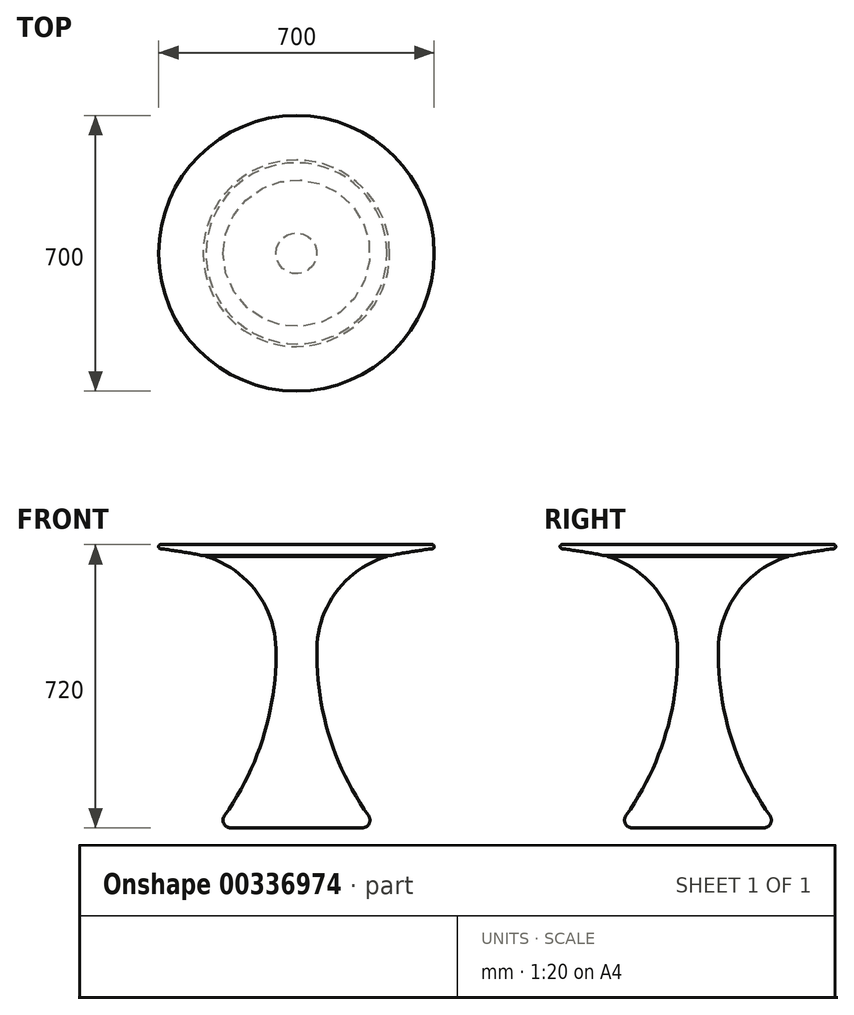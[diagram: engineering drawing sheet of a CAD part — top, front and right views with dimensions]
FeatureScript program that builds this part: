
annotation { "Feature Type Name" : "Feature", "Feature Type Description" : "" }
export const myFeature = defineFeature(function(context is Context, id is Id, definition is map)
    precondition{}
    {
        {
            var Q0;
            Q0=qCreatedBy(makeId("Front.planeOp"),FACE);
            var sketch = newSketch(context, id + "F0", { "sketchPlane" : qUnion([Q0])});
            skSolve(sketch);
        }
        {
            var Q0;
            Q0=qCreatedBy(makeId("Front.planeOp"),FACE);
            var sketch = newSketch(context, id + "F1", { "sketchPlane" : qUnion([Q0])});
            skLineSegment(sketch, "E0", {"start": v(350, 690) * mm, "end": v(120, 690) * mm});
            skLineSegment(sketch, "E1", {"start": v(350, 0) * mm, "end": v(350, 690) * mm});
            skLineSegment(sketch, "E2", {"start": v(350, 0) * mm, "end": v(183.46, 0) * mm});
            skArc(sketch, "E3", {"start": v(298, 455) * mm, "mid": v(247.32, 601.53) * mm, "end": v(120, 690) * mm});
            skArc(sketch, "E4", {"start": v(167.15, 31.57) * mm, "mid": v(266.46, 232.82) * mm, "end": v(298, 455) * mm});
            skPoint(sketch, "E5.visualSharp", {"position": v(143.4, 0) * mm});
            skArc(sketch, "E5.filletArc", {"start": v(167.15, 31.57) * mm, "mid": v(165.69, 10.82) * mm, "end": v(183.46, 0) * mm});
            skSolve(sketch);
        }
        {
            var Q0;
            Q0=qCreatedBy(makeId("Front.planeOp"),FACE);
            var sketch = newSketch(context, id + "F2", { "sketchPlane" : qUnion([Q0])});
            skLineSegment(sketch, "E6.0", {"start": v(350, 0) * mm, "end": v(350, 690) * mm});
            skSolve(sketch);
        }
        {
            var Q0;
            Q0 = qSketchRegion(id + "F1", true);
            var Q1;
            Q1=sQuery(id+"F2.wireOp",EDGE,"E6.0");
            revolve(context, id + "F3", {"entities" : qUnion([Q0]), "axis" : qUnion([Q1]), "revolveType" : RevolveType.FULL});
        }
        {
            var Q0;
            Q0=qCreatedBy(makeId("Front.planeOp"),FACE);
            var sketch = newSketch(context, id + "F4", { "sketchPlane" : qUnion([Q0])});
            skLineSegment(sketch, "E7", {"start": v(350, 720) * mm, "end": v(5, 720) * mm});
            skLineSegment(sketch, "E8", {"start": v(350, 720) * mm, "end": v(350, 692) * mm});
            skLineSegment(sketch, "E9", {"start": v(350, 692) * mm, "end": v(112.98, 692) * mm});
            skArc(sketch, "E10", {"start": v(112.98, 692) * mm, "mid": v(58.83, 701.66) * mm, "end": v(4.38, 709.46) * mm});
            skLineSegment(sketch, "E11", {"start": v(0, 715) * mm, "end": v(0, 714.42) * mm});
            skPoint(sketch, "E12.visualSharp", {"position": v(0, 710) * mm});
            skArc(sketch, "E12.filletArc", {"start": v(0, 714.42) * mm, "mid": v(1.25, 711.1) * mm, "end": v(4.38, 709.46) * mm});
            skPoint(sketch, "E13.visualSharp", {"position": v(0, 720) * mm});
            skArc(sketch, "E13.filletArc", {"start": v(5, 720) * mm, "mid": v(1.46, 718.54) * mm, "end": v(0, 715) * mm});
            skSolve(sketch);
        }
        {
            var Q0;
            Q0=makeQuery(id+"F4.imprint","IMPRINT",FACE,{"disambiguationData":[TD([[makeQuery(id+"F4.imprint","IMPRINT",EDGE,{"derivedFrom":sQuery(id+"F4.wireOp",EDGE,"E7")}),1.0]])]});
            var Q1;
            Q1=sQuery(id+"F4.wireOp",EDGE,"E8");
            revolve(context, id + "F5", {"entities" : qUnion([Q0]), "axis" : qUnion([Q1]), "revolveType" : RevolveType.FULL});
        }
    });
